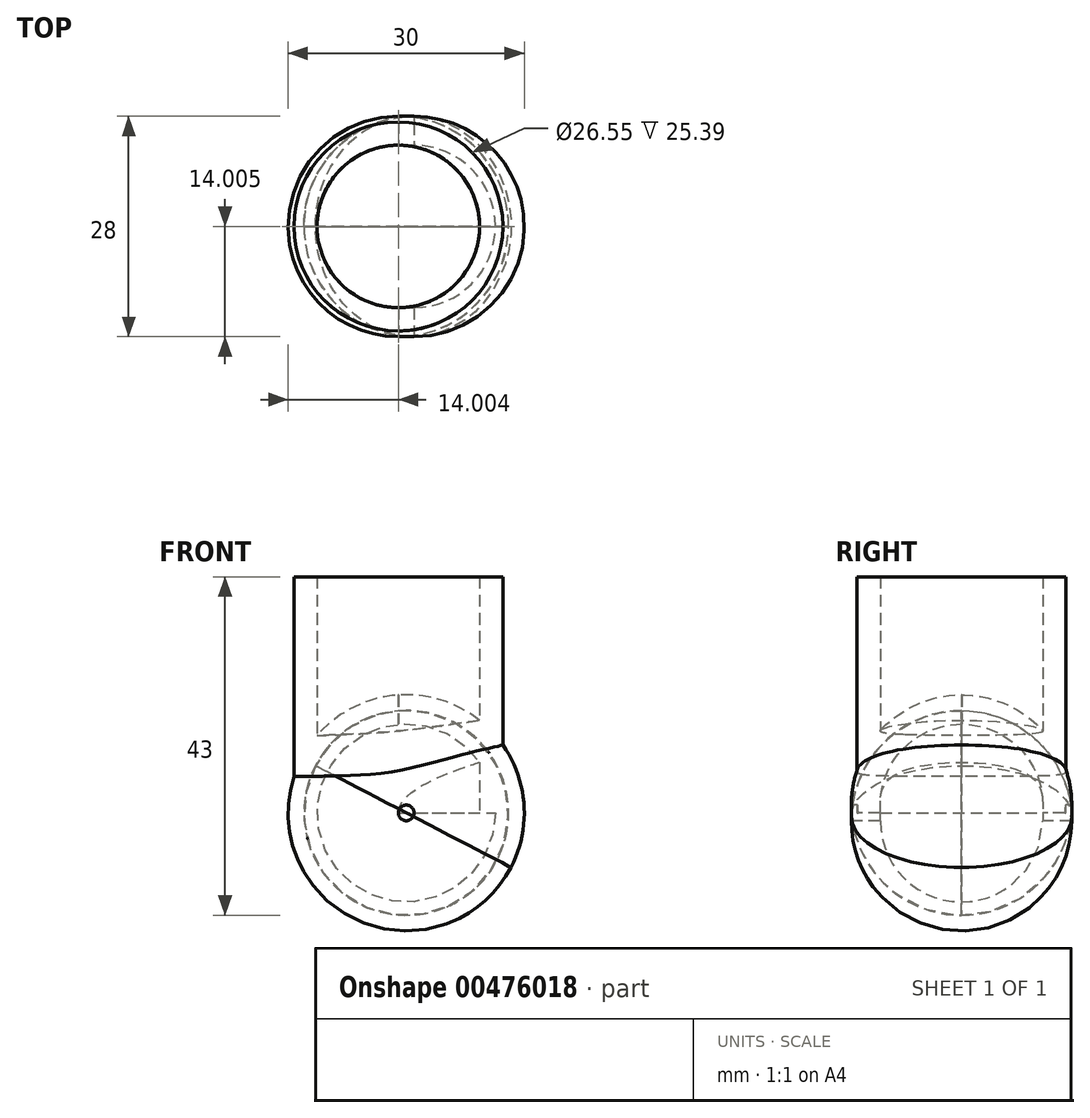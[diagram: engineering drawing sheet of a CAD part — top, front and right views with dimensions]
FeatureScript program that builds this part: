
annotation { "Feature Type Name" : "Feature", "Feature Type Description" : "" }
export const myFeature = defineFeature(function(context is Context, id is Id, definition is map)
    precondition{}
    {
        {
            var Q0;
            Q0=qCreatedBy(makeId("Top.planeOp"),FACE);
            var sketch = newSketch(context, id + "F0", { "sketchPlane" : qUnion([Q0])});
            skLineSegment(sketch, "E0", {"start": v(82.62, -61.93) * mm, "end": v(82.62, -33.93) * mm});
            skArc(sketch, "E1", {"start": v(82.62, -33.93) * mm, "mid": v(68.62, -47.93) * mm, "end": v(82.62, -61.93) * mm});
            skLineSegment(sketch, "E2.0", {"start": v(83.62, -107.64) * mm, "end": v(83.62, 106.68) * mm, "construction": true});
            skCircle(sketch, "E3", {"center": v(82.62, -47.93) * mm, "radius": 10.32 * mm});
            skCircle(sketch, "E4.0", {"center": v(82.62, -47.93) * mm, "radius": 13.27 * mm});
            skLineSegment(sketch, "E5", {"start": v(73.3, -52.35) * mm, "end": v(91.95, -43.5) * mm, "construction": true});
            skLineSegment(sketch, "E6", {"start": v(89.57, -40.3) * mm, "end": v(91.11, -37.72) * mm, "construction": true});
            skSolve(sketch);
        }
        {
            var Q0;
            Q0=makeQuery(id+"F0.imprint","IMPRINT",FACE,{"disambiguationData":[TD([[makeQuery(id+"F0.imprint","IMPRINT",EDGE,{"derivedFrom":sQuery(id+"F0.wireOp",EDGE,"E0")}),1.0]])]});
            var Q1;
            Q1=sQuery(id+"F0.wireOp",EDGE,"E2.0");
            revolve(context, id + "F1", {"entities" : qUnion([Q0]), "axis" : qUnion([Q1]), "revolveType" : RevolveType.FULL});
        }
        {
            var Q0;
            Q0=sQuery(id+"F0.wireOp",VERTEX,"E4.0.center");
            var Q1;
            Q1=makeQuery(id+"F1.opRevolve","SWEPT_BODY",BODY,{"disambiguationData":[OSD([sQuery(id+"F0.wireOp",EDGE,"E0"),sQuery(id+"F0.wireOp",EDGE,"E1"),sQuery(id+"F0.wireOp",EDGE,"E3")])]});
            hole(context, id + "F2", {"style" : HoleStyle.SIMPLE, "endStyle" : HoleEndStyle.BLIND, "oppositeDirection" : true, "holeDiameter" : 31 / 812.8 * mm, "holeDepth" : 90 * mm, "isTappedThrough" : true, "tappedDepth" : 12 * mm, "tapClearance" : 3, "locations" : qUnion([Q0]), "scope" : qUnion([Q1])});
        }
        {
            var Q0;
            {var subQ0=sQuery(id+"F0.wireOp",EDGE,"E4.0");var subQ1=sQuery(id+"F0.wireOp",EDGE,"E0");var subQ2=makeQuery(id+"F0.imprint","INTERSECT",VERTEX,{"disambiguationData":[OD(0.0)],"derivedFrom":[subQ1,subQ0]});Q0=makeQuery(id+"F0.imprint","IMPRINT",FACE,{"disambiguationData":[TD([[makeQuery(id+"F0.imprint","IMPRINT",EDGE,{"disambiguationData":[TD([[subQ2,-1.0]])],"derivedFrom":subQ1}),1.0]])]});}
            var Q1;
            {var subQ0=sQuery(id+"F0.wireOp",EDGE,"E4.0");var subQ1=sQuery(id+"F0.wireOp",EDGE,"E0");var subQ2=makeQuery(id+"F0.imprint","INTERSECT",VERTEX,{"disambiguationData":[OD(0.0)],"derivedFrom":[subQ1,subQ0]});Q1=makeQuery(id+"F0.imprint","IMPRINT",FACE,{"disambiguationData":[TD([[makeQuery(id+"F0.imprint","IMPRINT",EDGE,{"disambiguationData":[TD([[subQ2,-1.0]])],"derivedFrom":subQ1}),-1.0]])]});}
            extrude(context, id + "F3", {"entities" : qUnion([Q0, Q1]), "operationType" : NewBodyOperationType.ADD, "depth" : 30 * mm});
        }
    });
